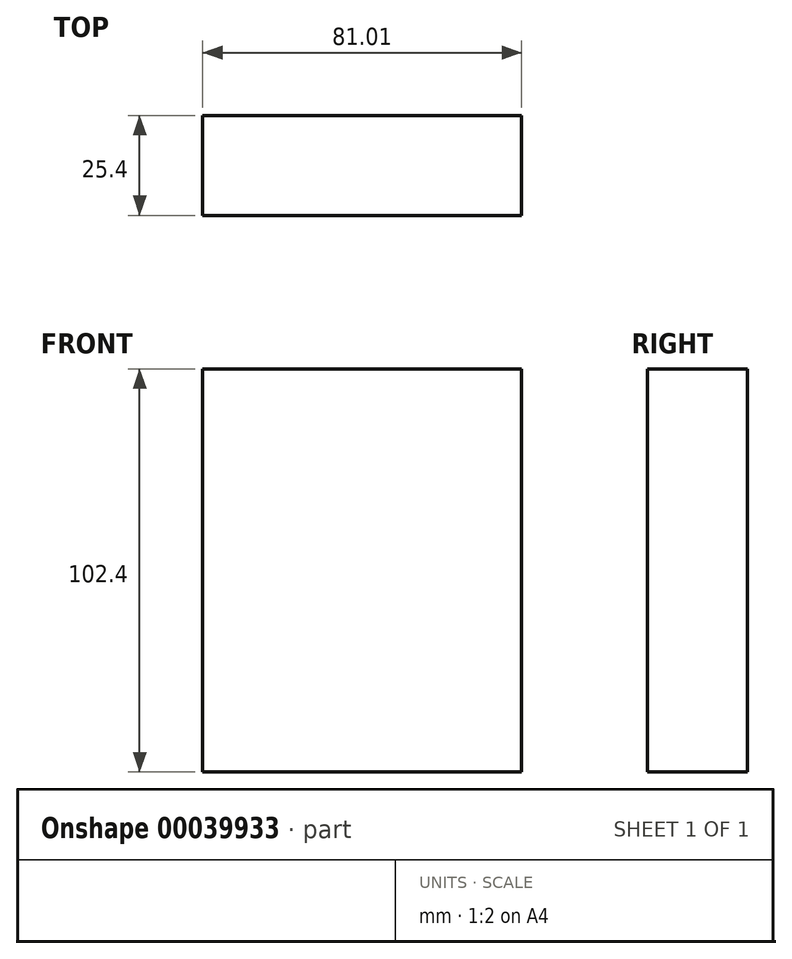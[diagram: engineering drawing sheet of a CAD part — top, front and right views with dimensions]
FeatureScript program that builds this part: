
annotation { "Feature Type Name" : "Feature", "Feature Type Description" : "" }
export const myFeature = defineFeature(function(context is Context, id is Id, definition is map)
    precondition{}
    {
        {
            var Q0;
            Q0=qCreatedBy(makeId("Front.planeOp"),FACE);
            var sketch = newSketch(context, id + "F0", { "sketchPlane" : qUnion([Q0])});
            skLineSegment(sketch, "E0.bottom", {"start": v(-55.43, 67.41) * mm, "end": v(25.58, 67.41) * mm});
            skLineSegment(sketch, "E0.top", {"start": v(-55.43, -34.99) * mm, "end": v(25.58, -34.99) * mm});
            skLineSegment(sketch, "E0.left", {"start": v(-55.43, 67.41) * mm, "end": v(-55.43, -34.99) * mm});
            skLineSegment(sketch, "E0.right", {"start": v(25.58, 67.41) * mm, "end": v(25.58, -34.99) * mm});
            skSolve(sketch);
        }
        {
            var Q0;
            Q0 = qSketchRegion(id + "F0", true);
            extrude(context, id + "F1", {"entities" : qUnion([Q0]), "depth" : 25.4 * mm});
        }
    });
